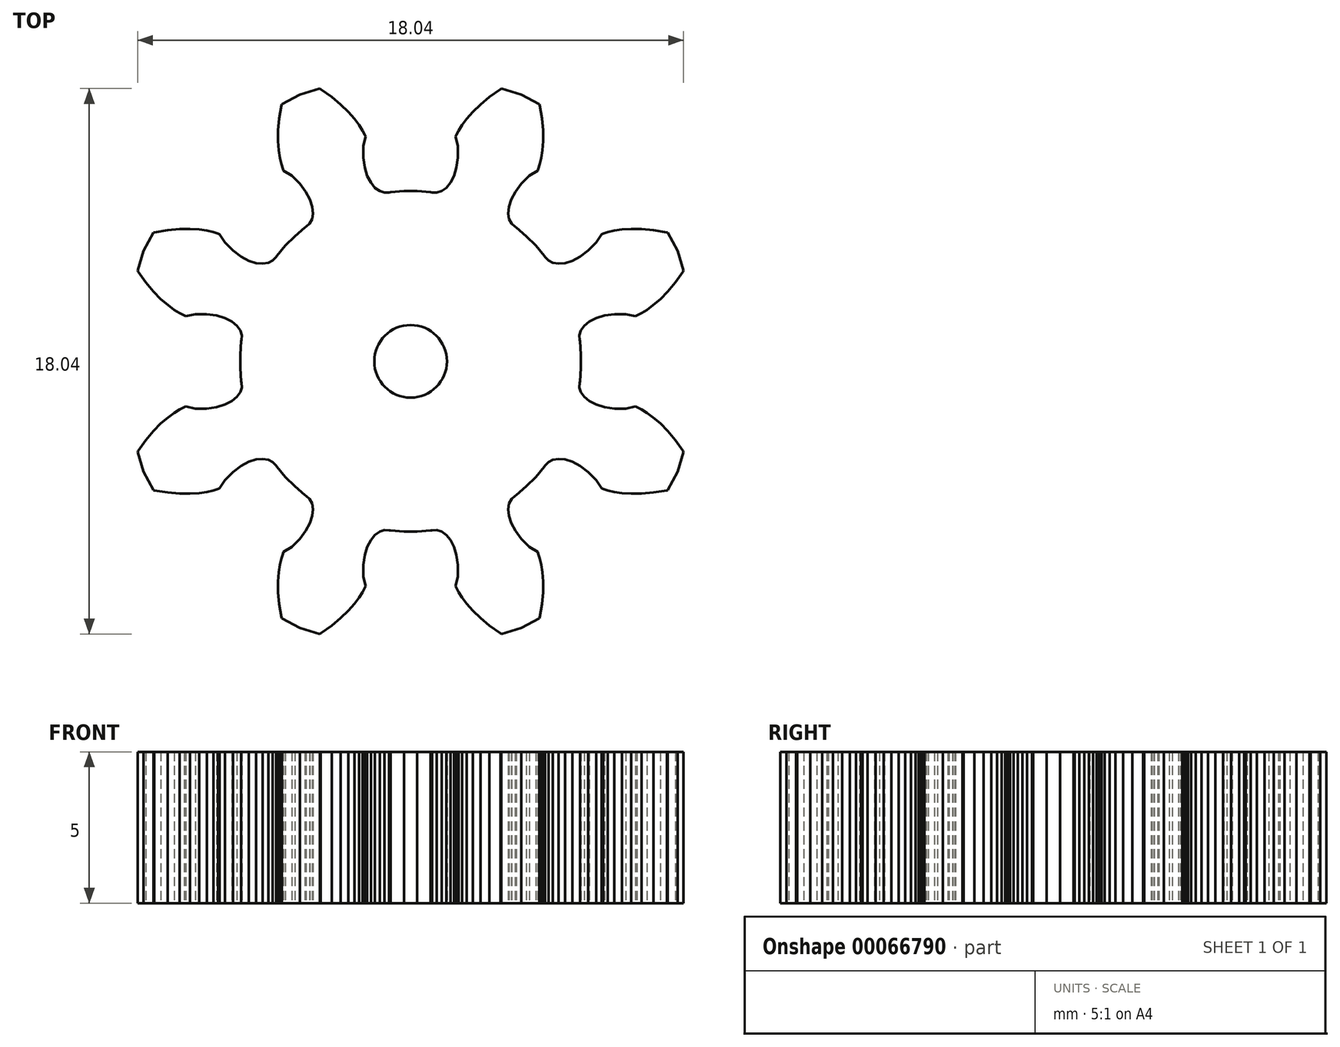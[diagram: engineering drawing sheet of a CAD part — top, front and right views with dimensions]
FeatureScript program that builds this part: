
annotation { "Feature Type Name" : "Feature", "Feature Type Description" : "" }
export const myFeature = defineFeature(function(context is Context, id is Id, definition is map)
    precondition{}
    {
        {
            var Q0;
            Q0=qCreatedBy(makeId("Top.planeOp"),FACE);
            var sketch = newSketch(context, id + "F0", { "sketchPlane" : qUnion([Q0])});
            skCircle(sketch, "E0", {"center": v(0, 0) * mm, "radius": 1.2 * mm});
            skLineSegment(sketch, "E1", {"start": v(-8.5, 4.26) * mm, "end": v(-8.82, 3.65) * mm});
            skLineSegment(sketch, "E2", {"start": v(-8.82, 3.65) * mm, "end": v(-9.02, 3) * mm});
            skLineSegment(sketch, "E3", {"start": v(-9.02, 3) * mm, "end": v(-9, 2.97) * mm});
            skLineSegment(sketch, "E4", {"start": v(-9, 2.97) * mm, "end": v(-8.75, 2.6) * mm});
            skLineSegment(sketch, "E5", {"start": v(-8.75, 2.6) * mm, "end": v(-8.5, 2.3) * mm});
            skLineSegment(sketch, "E6", {"start": v(-8.5, 2.3) * mm, "end": v(-8.25, 2.06) * mm});
            skLineSegment(sketch, "E7", {"start": v(-8.25, 2.06) * mm, "end": v(-8.02, 1.86) * mm});
            skLineSegment(sketch, "E8", {"start": v(-8.02, 1.86) * mm, "end": v(-7.81, 1.7) * mm});
            skLineSegment(sketch, "E9", {"start": v(-7.81, 1.7) * mm, "end": v(-7.63, 1.59) * mm});
            skLineSegment(sketch, "E10", {"start": v(-7.63, 1.59) * mm, "end": v(-7.48, 1.51) * mm});
            skLineSegment(sketch, "E11", {"start": v(-7.48, 1.51) * mm, "end": v(-7.43, 1.5) * mm});
            skLineSegment(sketch, "E12", {"start": v(-7.43, 1.5) * mm, "end": v(-7.11, 1.56) * mm});
            skLineSegment(sketch, "E13", {"start": v(-7.11, 1.56) * mm, "end": v(-6.74, 1.56) * mm});
            skLineSegment(sketch, "E14", {"start": v(-6.74, 1.56) * mm, "end": v(-6.41, 1.52) * mm});
            skLineSegment(sketch, "E15", {"start": v(-6.41, 1.52) * mm, "end": v(-6.13, 1.43) * mm});
            skLineSegment(sketch, "E16", {"start": v(-6.13, 1.43) * mm, "end": v(-5.9, 1.31) * mm});
            skLineSegment(sketch, "E17", {"start": v(-5.9, 1.31) * mm, "end": v(-5.74, 1.18) * mm});
            skLineSegment(sketch, "E18", {"start": v(-5.74, 1.18) * mm, "end": v(-5.63, 1.02) * mm});
            skLineSegment(sketch, "E19", {"start": v(-5.63, 1.02) * mm, "end": v(-5.58, 0.86) * mm});
            skLineSegment(sketch, "E20", {"start": v(-5.58, 0.86) * mm, "end": v(-5.59, 0.7) * mm});
            skLineSegment(sketch, "E21", {"start": v(-5.59, 0.7) * mm, "end": v(-5.6, 0.66) * mm});
            skLineSegment(sketch, "E22", {"start": v(-5.6, 0.66) * mm, "end": v(-5.63, 0.22) * mm});
            skLineSegment(sketch, "E23", {"start": v(-5.63, 0.22) * mm, "end": v(-5.63, -0.22) * mm});
            skLineSegment(sketch, "E24", {"start": v(-5.63, -0.22) * mm, "end": v(-5.6, -0.66) * mm});
            skLineSegment(sketch, "E25", {"start": v(-5.6, -0.66) * mm, "end": v(-5.59, -0.7) * mm});
            skLineSegment(sketch, "E26", {"start": v(-5.59, -0.7) * mm, "end": v(-5.58, -0.86) * mm});
            skLineSegment(sketch, "E27", {"start": v(-5.58, -0.86) * mm, "end": v(-5.63, -1.02) * mm});
            skLineSegment(sketch, "E28", {"start": v(-5.63, -1.02) * mm, "end": v(-5.74, -1.18) * mm});
            skLineSegment(sketch, "E29", {"start": v(-5.74, -1.18) * mm, "end": v(-5.9, -1.31) * mm});
            skLineSegment(sketch, "E30", {"start": v(-5.9, -1.31) * mm, "end": v(-6.13, -1.43) * mm});
            skLineSegment(sketch, "E31", {"start": v(-6.13, -1.43) * mm, "end": v(-6.41, -1.52) * mm});
            skLineSegment(sketch, "E32", {"start": v(-6.41, -1.52) * mm, "end": v(-6.74, -1.56) * mm});
            skLineSegment(sketch, "E33", {"start": v(-6.74, -1.56) * mm, "end": v(-7.11, -1.56) * mm});
            skLineSegment(sketch, "E34", {"start": v(-7.11, -1.56) * mm, "end": v(-7.43, -1.5) * mm});
            skLineSegment(sketch, "E35", {"start": v(-7.43, -1.5) * mm, "end": v(-7.48, -1.51) * mm});
            skLineSegment(sketch, "E36", {"start": v(-7.48, -1.51) * mm, "end": v(-7.63, -1.59) * mm});
            skLineSegment(sketch, "E37", {"start": v(-7.63, -1.59) * mm, "end": v(-7.81, -1.7) * mm});
            skLineSegment(sketch, "E38", {"start": v(-7.81, -1.7) * mm, "end": v(-8.02, -1.86) * mm});
            skLineSegment(sketch, "E39", {"start": v(-8.02, -1.86) * mm, "end": v(-8.25, -2.06) * mm});
            skLineSegment(sketch, "E40", {"start": v(-8.25, -2.06) * mm, "end": v(-8.5, -2.3) * mm});
            skLineSegment(sketch, "E41", {"start": v(-8.5, -2.3) * mm, "end": v(-8.75, -2.6) * mm});
            skLineSegment(sketch, "E42", {"start": v(-8.75, -2.6) * mm, "end": v(-9, -2.97) * mm});
            skLineSegment(sketch, "E43", {"start": v(-9, -2.97) * mm, "end": v(-9.02, -3) * mm});
            skLineSegment(sketch, "E44", {"start": v(-9.02, -3) * mm, "end": v(-8.82, -3.65) * mm});
            skLineSegment(sketch, "E45", {"start": v(-8.82, -3.65) * mm, "end": v(-8.5, -4.26) * mm});
            skLineSegment(sketch, "E46", {"start": v(-8.5, -4.26) * mm, "end": v(-8.46, -4.27) * mm});
            skLineSegment(sketch, "E47", {"start": v(-8.46, -4.27) * mm, "end": v(-8.03, -4.34) * mm});
            skLineSegment(sketch, "E48", {"start": v(-8.03, -4.34) * mm, "end": v(-7.64, -4.38) * mm});
            skLineSegment(sketch, "E49", {"start": v(-7.64, -4.38) * mm, "end": v(-7.29, -4.38) * mm});
            skLineSegment(sketch, "E50", {"start": v(-7.29, -4.38) * mm, "end": v(-6.98, -4.36) * mm});
            skLineSegment(sketch, "E51", {"start": v(-6.98, -4.36) * mm, "end": v(-6.73, -4.32) * mm});
            skLineSegment(sketch, "E52", {"start": v(-6.73, -4.32) * mm, "end": v(-6.52, -4.27) * mm});
            skLineSegment(sketch, "E53", {"start": v(-6.52, -4.27) * mm, "end": v(-6.36, -4.22) * mm});
            skLineSegment(sketch, "E54", {"start": v(-6.36, -4.22) * mm, "end": v(-6.3, -4.2) * mm});
            skLineSegment(sketch, "E55", {"start": v(-6.3, -4.2) * mm, "end": v(-6.14, -3.93) * mm});
            skLineSegment(sketch, "E56", {"start": v(-6.14, -3.93) * mm, "end": v(-5.87, -3.66) * mm});
            skLineSegment(sketch, "E57", {"start": v(-5.87, -3.66) * mm, "end": v(-5.6, -3.46) * mm});
            skLineSegment(sketch, "E58", {"start": v(-5.6, -3.46) * mm, "end": v(-5.35, -3.33) * mm});
            skLineSegment(sketch, "E59", {"start": v(-5.35, -3.33) * mm, "end": v(-5.1, -3.25) * mm});
            skLineSegment(sketch, "E60", {"start": v(-5.1, -3.25) * mm, "end": v(-4.89, -3.23) * mm});
            skLineSegment(sketch, "E61", {"start": v(-4.89, -3.23) * mm, "end": v(-4.7, -3.26) * mm});
            skLineSegment(sketch, "E62", {"start": v(-4.7, -3.26) * mm, "end": v(-4.56, -3.33) * mm});
            skLineSegment(sketch, "E63", {"start": v(-4.56, -3.33) * mm, "end": v(-4.45, -3.45) * mm});
            skLineSegment(sketch, "E64", {"start": v(-4.45, -3.45) * mm, "end": v(-4.42, -3.49) * mm});
            skLineSegment(sketch, "E65", {"start": v(-4.42, -3.49) * mm, "end": v(-4.14, -3.82) * mm});
            skLineSegment(sketch, "E66", {"start": v(-4.14, -3.82) * mm, "end": v(-3.82, -4.14) * mm});
            skLineSegment(sketch, "E67", {"start": v(-3.82, -4.14) * mm, "end": v(-3.49, -4.42) * mm});
            skLineSegment(sketch, "E68", {"start": v(-3.49, -4.42) * mm, "end": v(-3.45, -4.45) * mm});
            skLineSegment(sketch, "E69", {"start": v(-3.45, -4.45) * mm, "end": v(-3.33, -4.56) * mm});
            skLineSegment(sketch, "E70", {"start": v(-3.33, -4.56) * mm, "end": v(-3.26, -4.7) * mm});
            skLineSegment(sketch, "E71", {"start": v(-3.26, -4.7) * mm, "end": v(-3.23, -4.89) * mm});
            skLineSegment(sketch, "E72", {"start": v(-3.23, -4.89) * mm, "end": v(-3.25, -5.1) * mm});
            skLineSegment(sketch, "E73", {"start": v(-3.25, -5.1) * mm, "end": v(-3.33, -5.35) * mm});
            skLineSegment(sketch, "E74", {"start": v(-3.33, -5.35) * mm, "end": v(-3.46, -5.6) * mm});
            skLineSegment(sketch, "E75", {"start": v(-3.46, -5.6) * mm, "end": v(-3.66, -5.87) * mm});
            skLineSegment(sketch, "E76", {"start": v(-3.66, -5.87) * mm, "end": v(-3.93, -6.14) * mm});
            skLineSegment(sketch, "E77", {"start": v(-3.93, -6.14) * mm, "end": v(-4.2, -6.3) * mm});
            skLineSegment(sketch, "E78", {"start": v(-4.2, -6.3) * mm, "end": v(-4.22, -6.36) * mm});
            skLineSegment(sketch, "E79", {"start": v(-4.22, -6.36) * mm, "end": v(-4.27, -6.52) * mm});
            skLineSegment(sketch, "E80", {"start": v(-4.27, -6.52) * mm, "end": v(-4.32, -6.73) * mm});
            skLineSegment(sketch, "E81", {"start": v(-4.32, -6.73) * mm, "end": v(-4.36, -6.98) * mm});
            skLineSegment(sketch, "E82", {"start": v(-4.36, -6.98) * mm, "end": v(-4.38, -7.29) * mm});
            skLineSegment(sketch, "E83", {"start": v(-4.38, -7.29) * mm, "end": v(-4.38, -7.64) * mm});
            skLineSegment(sketch, "E84", {"start": v(-4.38, -7.64) * mm, "end": v(-4.34, -8.03) * mm});
            skLineSegment(sketch, "E85", {"start": v(-4.34, -8.03) * mm, "end": v(-4.27, -8.46) * mm});
            skLineSegment(sketch, "E86", {"start": v(-4.27, -8.46) * mm, "end": v(-4.26, -8.5) * mm});
            skLineSegment(sketch, "E87", {"start": v(-4.26, -8.5) * mm, "end": v(-3.65, -8.82) * mm});
            skLineSegment(sketch, "E88", {"start": v(-3.65, -8.82) * mm, "end": v(-3, -9.02) * mm});
            skLineSegment(sketch, "E89", {"start": v(-3, -9.02) * mm, "end": v(-2.97, -9) * mm});
            skLineSegment(sketch, "E90", {"start": v(-2.97, -9) * mm, "end": v(-2.6, -8.75) * mm});
            skLineSegment(sketch, "E91", {"start": v(-2.6, -8.75) * mm, "end": v(-2.3, -8.5) * mm});
            skLineSegment(sketch, "E92", {"start": v(-2.3, -8.5) * mm, "end": v(-2.06, -8.25) * mm});
            skLineSegment(sketch, "E93", {"start": v(-2.06, -8.25) * mm, "end": v(-1.86, -8.02) * mm});
            skLineSegment(sketch, "E94", {"start": v(-1.86, -8.02) * mm, "end": v(-1.7, -7.81) * mm});
            skLineSegment(sketch, "E95", {"start": v(-1.7, -7.81) * mm, "end": v(-1.59, -7.63) * mm});
            skLineSegment(sketch, "E96", {"start": v(-1.59, -7.63) * mm, "end": v(-1.51, -7.48) * mm});
            skLineSegment(sketch, "E97", {"start": v(-1.51, -7.48) * mm, "end": v(-1.5, -7.43) * mm});
            skLineSegment(sketch, "E98", {"start": v(-1.5, -7.43) * mm, "end": v(-1.56, -7.11) * mm});
            skLineSegment(sketch, "E99", {"start": v(-1.56, -7.11) * mm, "end": v(-1.56, -6.74) * mm});
            skLineSegment(sketch, "E100", {"start": v(-1.56, -6.74) * mm, "end": v(-1.52, -6.41) * mm});
            skLineSegment(sketch, "E101", {"start": v(-1.52, -6.41) * mm, "end": v(-1.43, -6.13) * mm});
            skLineSegment(sketch, "E102", {"start": v(-1.43, -6.13) * mm, "end": v(-1.31, -5.9) * mm});
            skLineSegment(sketch, "E103", {"start": v(-1.31, -5.9) * mm, "end": v(-1.18, -5.74) * mm});
            skLineSegment(sketch, "E104", {"start": v(-1.18, -5.74) * mm, "end": v(-1.02, -5.63) * mm});
            skLineSegment(sketch, "E105", {"start": v(-1.02, -5.63) * mm, "end": v(-0.86, -5.58) * mm});
            skLineSegment(sketch, "E106", {"start": v(-0.86, -5.58) * mm, "end": v(-0.7, -5.59) * mm});
            skLineSegment(sketch, "E107", {"start": v(-0.7, -5.59) * mm, "end": v(-0.66, -5.6) * mm});
            skLineSegment(sketch, "E108", {"start": v(-0.66, -5.6) * mm, "end": v(-0.22, -5.63) * mm});
            skLineSegment(sketch, "E109", {"start": v(-0.22, -5.63) * mm, "end": v(0.22, -5.63) * mm});
            skLineSegment(sketch, "E110", {"start": v(0.22, -5.63) * mm, "end": v(0.66, -5.6) * mm});
            skLineSegment(sketch, "E111", {"start": v(0.66, -5.6) * mm, "end": v(0.7, -5.59) * mm});
            skLineSegment(sketch, "E112", {"start": v(0.7, -5.59) * mm, "end": v(0.86, -5.58) * mm});
            skLineSegment(sketch, "E113", {"start": v(0.86, -5.58) * mm, "end": v(1.02, -5.63) * mm});
            skLineSegment(sketch, "E114", {"start": v(1.02, -5.63) * mm, "end": v(1.18, -5.74) * mm});
            skLineSegment(sketch, "E115", {"start": v(1.18, -5.74) * mm, "end": v(1.31, -5.9) * mm});
            skLineSegment(sketch, "E116", {"start": v(1.31, -5.9) * mm, "end": v(1.43, -6.13) * mm});
            skLineSegment(sketch, "E117", {"start": v(1.43, -6.13) * mm, "end": v(1.52, -6.41) * mm});
            skLineSegment(sketch, "E118", {"start": v(1.52, -6.41) * mm, "end": v(1.56, -6.74) * mm});
            skLineSegment(sketch, "E119", {"start": v(1.56, -6.74) * mm, "end": v(1.56, -7.11) * mm});
            skLineSegment(sketch, "E120", {"start": v(1.56, -7.11) * mm, "end": v(1.5, -7.43) * mm});
            skLineSegment(sketch, "E121", {"start": v(1.5, -7.43) * mm, "end": v(1.51, -7.48) * mm});
            skLineSegment(sketch, "E122", {"start": v(1.51, -7.48) * mm, "end": v(1.59, -7.63) * mm});
            skLineSegment(sketch, "E123", {"start": v(1.59, -7.63) * mm, "end": v(1.7, -7.81) * mm});
            skLineSegment(sketch, "E124", {"start": v(1.7, -7.81) * mm, "end": v(1.86, -8.02) * mm});
            skLineSegment(sketch, "E125", {"start": v(1.86, -8.02) * mm, "end": v(2.06, -8.25) * mm});
            skLineSegment(sketch, "E126", {"start": v(2.06, -8.25) * mm, "end": v(2.3, -8.5) * mm});
            skLineSegment(sketch, "E127", {"start": v(2.3, -8.5) * mm, "end": v(2.6, -8.75) * mm});
            skLineSegment(sketch, "E128", {"start": v(2.6, -8.75) * mm, "end": v(2.97, -9) * mm});
            skLineSegment(sketch, "E129", {"start": v(2.97, -9) * mm, "end": v(3, -9.02) * mm});
            skLineSegment(sketch, "E130", {"start": v(3, -9.02) * mm, "end": v(3.65, -8.82) * mm});
            skLineSegment(sketch, "E131", {"start": v(3.65, -8.82) * mm, "end": v(4.26, -8.5) * mm});
            skLineSegment(sketch, "E132", {"start": v(4.26, -8.5) * mm, "end": v(4.27, -8.46) * mm});
            skLineSegment(sketch, "E133", {"start": v(4.27, -8.46) * mm, "end": v(4.34, -8.03) * mm});
            skLineSegment(sketch, "E134", {"start": v(4.34, -8.03) * mm, "end": v(4.38, -7.64) * mm});
            skLineSegment(sketch, "E135", {"start": v(4.38, -7.64) * mm, "end": v(4.38, -7.29) * mm});
            skLineSegment(sketch, "E136", {"start": v(4.38, -7.29) * mm, "end": v(4.36, -6.98) * mm});
            skLineSegment(sketch, "E137", {"start": v(4.36, -6.98) * mm, "end": v(4.32, -6.73) * mm});
            skLineSegment(sketch, "E138", {"start": v(4.32, -6.73) * mm, "end": v(4.27, -6.52) * mm});
            skLineSegment(sketch, "E139", {"start": v(4.27, -6.52) * mm, "end": v(4.22, -6.36) * mm});
            skLineSegment(sketch, "E140", {"start": v(4.22, -6.36) * mm, "end": v(4.2, -6.3) * mm});
            skLineSegment(sketch, "E141", {"start": v(4.2, -6.3) * mm, "end": v(3.93, -6.14) * mm});
            skLineSegment(sketch, "E142", {"start": v(3.93, -6.14) * mm, "end": v(3.66, -5.87) * mm});
            skLineSegment(sketch, "E143", {"start": v(3.66, -5.87) * mm, "end": v(3.46, -5.6) * mm});
            skLineSegment(sketch, "E144", {"start": v(3.46, -5.6) * mm, "end": v(3.33, -5.35) * mm});
            skLineSegment(sketch, "E145", {"start": v(3.33, -5.35) * mm, "end": v(3.25, -5.1) * mm});
            skLineSegment(sketch, "E146", {"start": v(3.25, -5.1) * mm, "end": v(3.23, -4.89) * mm});
            skLineSegment(sketch, "E147", {"start": v(3.23, -4.89) * mm, "end": v(3.26, -4.7) * mm});
            skLineSegment(sketch, "E148", {"start": v(3.26, -4.7) * mm, "end": v(3.33, -4.56) * mm});
            skLineSegment(sketch, "E149", {"start": v(3.33, -4.56) * mm, "end": v(3.45, -4.45) * mm});
            skLineSegment(sketch, "E150", {"start": v(3.45, -4.45) * mm, "end": v(3.49, -4.42) * mm});
            skLineSegment(sketch, "E151", {"start": v(3.49, -4.42) * mm, "end": v(3.82, -4.14) * mm});
            skLineSegment(sketch, "E152", {"start": v(3.82, -4.14) * mm, "end": v(4.14, -3.82) * mm});
            skLineSegment(sketch, "E153", {"start": v(4.14, -3.82) * mm, "end": v(4.42, -3.49) * mm});
            skLineSegment(sketch, "E154", {"start": v(4.42, -3.49) * mm, "end": v(4.45, -3.45) * mm});
            skLineSegment(sketch, "E155", {"start": v(4.45, -3.45) * mm, "end": v(4.56, -3.33) * mm});
            skLineSegment(sketch, "E156", {"start": v(4.56, -3.33) * mm, "end": v(4.7, -3.26) * mm});
            skLineSegment(sketch, "E157", {"start": v(4.7, -3.26) * mm, "end": v(4.89, -3.23) * mm});
            skLineSegment(sketch, "E158", {"start": v(4.89, -3.23) * mm, "end": v(5.1, -3.25) * mm});
            skLineSegment(sketch, "E159", {"start": v(5.1, -3.25) * mm, "end": v(5.35, -3.33) * mm});
            skLineSegment(sketch, "E160", {"start": v(5.35, -3.33) * mm, "end": v(5.6, -3.46) * mm});
            skLineSegment(sketch, "E161", {"start": v(5.6, -3.46) * mm, "end": v(5.87, -3.66) * mm});
            skLineSegment(sketch, "E162", {"start": v(5.87, -3.66) * mm, "end": v(6.14, -3.93) * mm});
            skLineSegment(sketch, "E163", {"start": v(6.14, -3.93) * mm, "end": v(6.3, -4.2) * mm});
            skLineSegment(sketch, "E164", {"start": v(6.3, -4.2) * mm, "end": v(6.36, -4.22) * mm});
            skLineSegment(sketch, "E165", {"start": v(6.36, -4.22) * mm, "end": v(6.52, -4.27) * mm});
            skLineSegment(sketch, "E166", {"start": v(6.52, -4.27) * mm, "end": v(6.73, -4.32) * mm});
            skLineSegment(sketch, "E167", {"start": v(6.73, -4.32) * mm, "end": v(6.98, -4.36) * mm});
            skLineSegment(sketch, "E168", {"start": v(6.98, -4.36) * mm, "end": v(7.29, -4.38) * mm});
            skLineSegment(sketch, "E169", {"start": v(7.29, -4.38) * mm, "end": v(7.64, -4.38) * mm});
            skLineSegment(sketch, "E170", {"start": v(7.64, -4.38) * mm, "end": v(8.03, -4.34) * mm});
            skLineSegment(sketch, "E171", {"start": v(8.03, -4.34) * mm, "end": v(8.46, -4.27) * mm});
            skLineSegment(sketch, "E172", {"start": v(8.46, -4.27) * mm, "end": v(8.5, -4.26) * mm});
            skLineSegment(sketch, "E173", {"start": v(8.5, -4.26) * mm, "end": v(8.82, -3.65) * mm});
            skLineSegment(sketch, "E174", {"start": v(8.82, -3.65) * mm, "end": v(9.02, -3) * mm});
            skLineSegment(sketch, "E175", {"start": v(9.02, -3) * mm, "end": v(9, -2.97) * mm});
            skLineSegment(sketch, "E176", {"start": v(9, -2.97) * mm, "end": v(8.75, -2.6) * mm});
            skLineSegment(sketch, "E177", {"start": v(8.75, -2.6) * mm, "end": v(8.5, -2.3) * mm});
            skLineSegment(sketch, "E178", {"start": v(8.5, -2.3) * mm, "end": v(8.25, -2.06) * mm});
            skLineSegment(sketch, "E179", {"start": v(8.25, -2.06) * mm, "end": v(8.02, -1.86) * mm});
            skLineSegment(sketch, "E180", {"start": v(8.02, -1.86) * mm, "end": v(7.81, -1.7) * mm});
            skLineSegment(sketch, "E181", {"start": v(7.81, -1.7) * mm, "end": v(7.63, -1.59) * mm});
            skLineSegment(sketch, "E182", {"start": v(7.63, -1.59) * mm, "end": v(7.48, -1.51) * mm});
            skLineSegment(sketch, "E183", {"start": v(7.48, -1.51) * mm, "end": v(7.43, -1.5) * mm});
            skLineSegment(sketch, "E184", {"start": v(7.43, -1.5) * mm, "end": v(7.11, -1.56) * mm});
            skLineSegment(sketch, "E185", {"start": v(7.11, -1.56) * mm, "end": v(6.74, -1.56) * mm});
            skLineSegment(sketch, "E186", {"start": v(6.74, -1.56) * mm, "end": v(6.41, -1.52) * mm});
            skLineSegment(sketch, "E187", {"start": v(6.41, -1.52) * mm, "end": v(6.13, -1.43) * mm});
            skLineSegment(sketch, "E188", {"start": v(6.13, -1.43) * mm, "end": v(5.9, -1.31) * mm});
            skLineSegment(sketch, "E189", {"start": v(5.9, -1.31) * mm, "end": v(5.74, -1.18) * mm});
            skLineSegment(sketch, "E190", {"start": v(5.74, -1.18) * mm, "end": v(5.63, -1.02) * mm});
            skLineSegment(sketch, "E191", {"start": v(5.63, -1.02) * mm, "end": v(5.58, -0.86) * mm});
            skLineSegment(sketch, "E192", {"start": v(5.58, -0.86) * mm, "end": v(5.59, -0.7) * mm});
            skLineSegment(sketch, "E193", {"start": v(5.59, -0.7) * mm, "end": v(5.6, -0.66) * mm});
            skLineSegment(sketch, "E194", {"start": v(5.6, -0.66) * mm, "end": v(5.63, -0.22) * mm});
            skLineSegment(sketch, "E195", {"start": v(5.63, -0.22) * mm, "end": v(5.63, 0.22) * mm});
            skLineSegment(sketch, "E196", {"start": v(5.63, 0.22) * mm, "end": v(5.6, 0.66) * mm});
            skLineSegment(sketch, "E197", {"start": v(5.6, 0.66) * mm, "end": v(5.59, 0.7) * mm});
            skLineSegment(sketch, "E198", {"start": v(5.59, 0.7) * mm, "end": v(5.58, 0.86) * mm});
            skLineSegment(sketch, "E199", {"start": v(5.58, 0.86) * mm, "end": v(5.63, 1.02) * mm});
            skLineSegment(sketch, "E200", {"start": v(5.63, 1.02) * mm, "end": v(5.74, 1.18) * mm});
            skLineSegment(sketch, "E201", {"start": v(5.74, 1.18) * mm, "end": v(5.9, 1.31) * mm});
            skLineSegment(sketch, "E202", {"start": v(5.9, 1.31) * mm, "end": v(6.13, 1.43) * mm});
            skLineSegment(sketch, "E203", {"start": v(6.13, 1.43) * mm, "end": v(6.41, 1.52) * mm});
            skLineSegment(sketch, "E204", {"start": v(6.41, 1.52) * mm, "end": v(6.74, 1.56) * mm});
            skLineSegment(sketch, "E205", {"start": v(6.74, 1.56) * mm, "end": v(7.11, 1.56) * mm});
            skLineSegment(sketch, "E206", {"start": v(7.11, 1.56) * mm, "end": v(7.43, 1.5) * mm});
            skLineSegment(sketch, "E207", {"start": v(7.43, 1.5) * mm, "end": v(7.48, 1.51) * mm});
            skLineSegment(sketch, "E208", {"start": v(7.48, 1.51) * mm, "end": v(7.63, 1.59) * mm});
            skLineSegment(sketch, "E209", {"start": v(7.63, 1.59) * mm, "end": v(7.81, 1.7) * mm});
            skLineSegment(sketch, "E210", {"start": v(7.81, 1.7) * mm, "end": v(8.02, 1.86) * mm});
            skLineSegment(sketch, "E211", {"start": v(8.02, 1.86) * mm, "end": v(8.25, 2.06) * mm});
            skLineSegment(sketch, "E212", {"start": v(8.25, 2.06) * mm, "end": v(8.5, 2.3) * mm});
            skLineSegment(sketch, "E213", {"start": v(8.5, 2.3) * mm, "end": v(8.75, 2.6) * mm});
            skLineSegment(sketch, "E214", {"start": v(8.75, 2.6) * mm, "end": v(9, 2.97) * mm});
            skLineSegment(sketch, "E215", {"start": v(9, 2.97) * mm, "end": v(9.02, 3) * mm});
            skLineSegment(sketch, "E216", {"start": v(9.02, 3) * mm, "end": v(8.82, 3.65) * mm});
            skLineSegment(sketch, "E217", {"start": v(8.82, 3.65) * mm, "end": v(8.5, 4.26) * mm});
            skLineSegment(sketch, "E218", {"start": v(8.5, 4.26) * mm, "end": v(8.46, 4.27) * mm});
            skLineSegment(sketch, "E219", {"start": v(8.46, 4.27) * mm, "end": v(8.03, 4.34) * mm});
            skLineSegment(sketch, "E220", {"start": v(8.03, 4.34) * mm, "end": v(7.64, 4.38) * mm});
            skLineSegment(sketch, "E221", {"start": v(7.64, 4.38) * mm, "end": v(7.29, 4.38) * mm});
            skLineSegment(sketch, "E222", {"start": v(7.29, 4.38) * mm, "end": v(6.98, 4.36) * mm});
            skLineSegment(sketch, "E223", {"start": v(6.98, 4.36) * mm, "end": v(6.73, 4.32) * mm});
            skLineSegment(sketch, "E224", {"start": v(6.73, 4.32) * mm, "end": v(6.52, 4.27) * mm});
            skLineSegment(sketch, "E225", {"start": v(6.52, 4.27) * mm, "end": v(6.36, 4.22) * mm});
            skLineSegment(sketch, "E226", {"start": v(6.36, 4.22) * mm, "end": v(6.3, 4.2) * mm});
            skLineSegment(sketch, "E227", {"start": v(6.3, 4.2) * mm, "end": v(6.14, 3.93) * mm});
            skLineSegment(sketch, "E228", {"start": v(6.14, 3.93) * mm, "end": v(5.87, 3.66) * mm});
            skLineSegment(sketch, "E229", {"start": v(5.87, 3.66) * mm, "end": v(5.6, 3.46) * mm});
            skLineSegment(sketch, "E230", {"start": v(5.6, 3.46) * mm, "end": v(5.35, 3.33) * mm});
            skLineSegment(sketch, "E231", {"start": v(5.35, 3.33) * mm, "end": v(5.1, 3.25) * mm});
            skLineSegment(sketch, "E232", {"start": v(5.1, 3.25) * mm, "end": v(4.89, 3.23) * mm});
            skLineSegment(sketch, "E233", {"start": v(4.89, 3.23) * mm, "end": v(4.7, 3.26) * mm});
            skLineSegment(sketch, "E234", {"start": v(4.7, 3.26) * mm, "end": v(4.56, 3.33) * mm});
            skLineSegment(sketch, "E235", {"start": v(4.56, 3.33) * mm, "end": v(4.45, 3.45) * mm});
            skLineSegment(sketch, "E236", {"start": v(4.45, 3.45) * mm, "end": v(4.42, 3.49) * mm});
            skLineSegment(sketch, "E237", {"start": v(4.42, 3.49) * mm, "end": v(4.14, 3.82) * mm});
            skLineSegment(sketch, "E238", {"start": v(4.14, 3.82) * mm, "end": v(3.82, 4.14) * mm});
            skLineSegment(sketch, "E239", {"start": v(3.82, 4.14) * mm, "end": v(3.49, 4.42) * mm});
            skLineSegment(sketch, "E240", {"start": v(3.49, 4.42) * mm, "end": v(3.45, 4.45) * mm});
            skLineSegment(sketch, "E241", {"start": v(3.45, 4.45) * mm, "end": v(3.33, 4.56) * mm});
            skLineSegment(sketch, "E242", {"start": v(3.33, 4.56) * mm, "end": v(3.26, 4.7) * mm});
            skLineSegment(sketch, "E243", {"start": v(3.26, 4.7) * mm, "end": v(3.23, 4.89) * mm});
            skLineSegment(sketch, "E244", {"start": v(3.23, 4.89) * mm, "end": v(3.25, 5.1) * mm});
            skLineSegment(sketch, "E245", {"start": v(3.25, 5.1) * mm, "end": v(3.33, 5.35) * mm});
            skLineSegment(sketch, "E246", {"start": v(3.33, 5.35) * mm, "end": v(3.46, 5.6) * mm});
            skLineSegment(sketch, "E247", {"start": v(3.46, 5.6) * mm, "end": v(3.66, 5.87) * mm});
            skLineSegment(sketch, "E248", {"start": v(3.66, 5.87) * mm, "end": v(3.93, 6.14) * mm});
            skLineSegment(sketch, "E249", {"start": v(3.93, 6.14) * mm, "end": v(4.2, 6.3) * mm});
            skLineSegment(sketch, "E250", {"start": v(4.2, 6.3) * mm, "end": v(4.22, 6.36) * mm});
            skLineSegment(sketch, "E251", {"start": v(4.22, 6.36) * mm, "end": v(4.27, 6.52) * mm});
            skLineSegment(sketch, "E252", {"start": v(4.27, 6.52) * mm, "end": v(4.32, 6.73) * mm});
            skLineSegment(sketch, "E253", {"start": v(4.32, 6.73) * mm, "end": v(4.36, 6.98) * mm});
            skLineSegment(sketch, "E254", {"start": v(4.36, 6.98) * mm, "end": v(4.38, 7.29) * mm});
            skLineSegment(sketch, "E255", {"start": v(4.38, 7.29) * mm, "end": v(4.38, 7.64) * mm});
            skLineSegment(sketch, "E256", {"start": v(4.38, 7.64) * mm, "end": v(4.34, 8.03) * mm});
            skLineSegment(sketch, "E257", {"start": v(4.34, 8.03) * mm, "end": v(4.27, 8.46) * mm});
            skLineSegment(sketch, "E258", {"start": v(4.27, 8.46) * mm, "end": v(4.26, 8.5) * mm});
            skLineSegment(sketch, "E259", {"start": v(4.26, 8.5) * mm, "end": v(3.65, 8.82) * mm});
            skLineSegment(sketch, "E260", {"start": v(3.65, 8.82) * mm, "end": v(3, 9.02) * mm});
            skLineSegment(sketch, "E261", {"start": v(3, 9.02) * mm, "end": v(2.97, 9) * mm});
            skLineSegment(sketch, "E262", {"start": v(2.97, 9) * mm, "end": v(2.6, 8.75) * mm});
            skLineSegment(sketch, "E263", {"start": v(2.6, 8.75) * mm, "end": v(2.3, 8.5) * mm});
            skLineSegment(sketch, "E264", {"start": v(2.3, 8.5) * mm, "end": v(2.06, 8.25) * mm});
            skLineSegment(sketch, "E265", {"start": v(2.06, 8.25) * mm, "end": v(1.86, 8.02) * mm});
            skLineSegment(sketch, "E266", {"start": v(1.86, 8.02) * mm, "end": v(1.7, 7.81) * mm});
            skLineSegment(sketch, "E267", {"start": v(1.7, 7.81) * mm, "end": v(1.59, 7.63) * mm});
            skLineSegment(sketch, "E268", {"start": v(1.59, 7.63) * mm, "end": v(1.51, 7.48) * mm});
            skLineSegment(sketch, "E269", {"start": v(1.51, 7.48) * mm, "end": v(1.5, 7.43) * mm});
            skLineSegment(sketch, "E270", {"start": v(1.5, 7.43) * mm, "end": v(1.56, 7.11) * mm});
            skLineSegment(sketch, "E271", {"start": v(1.56, 7.11) * mm, "end": v(1.56, 6.74) * mm});
            skLineSegment(sketch, "E272", {"start": v(1.56, 6.74) * mm, "end": v(1.52, 6.41) * mm});
            skLineSegment(sketch, "E273", {"start": v(1.52, 6.41) * mm, "end": v(1.43, 6.13) * mm});
            skLineSegment(sketch, "E274", {"start": v(1.43, 6.13) * mm, "end": v(1.31, 5.9) * mm});
            skLineSegment(sketch, "E275", {"start": v(1.31, 5.9) * mm, "end": v(1.18, 5.74) * mm});
            skLineSegment(sketch, "E276", {"start": v(1.18, 5.74) * mm, "end": v(1.02, 5.63) * mm});
            skLineSegment(sketch, "E277", {"start": v(1.02, 5.63) * mm, "end": v(0.86, 5.58) * mm});
            skLineSegment(sketch, "E278", {"start": v(0.86, 5.58) * mm, "end": v(0.7, 5.59) * mm});
            skLineSegment(sketch, "E279", {"start": v(0.7, 5.59) * mm, "end": v(0.66, 5.6) * mm});
            skLineSegment(sketch, "E280", {"start": v(0.66, 5.6) * mm, "end": v(0.22, 5.63) * mm});
            skLineSegment(sketch, "E281", {"start": v(0.22, 5.63) * mm, "end": v(-0.22, 5.63) * mm});
            skLineSegment(sketch, "E282", {"start": v(-0.22, 5.63) * mm, "end": v(-0.66, 5.6) * mm});
            skLineSegment(sketch, "E283", {"start": v(-0.66, 5.6) * mm, "end": v(-0.7, 5.59) * mm});
            skLineSegment(sketch, "E284", {"start": v(-0.7, 5.59) * mm, "end": v(-0.86, 5.58) * mm});
            skLineSegment(sketch, "E285", {"start": v(-0.86, 5.58) * mm, "end": v(-1.02, 5.63) * mm});
            skLineSegment(sketch, "E286", {"start": v(-1.02, 5.63) * mm, "end": v(-1.18, 5.74) * mm});
            skLineSegment(sketch, "E287", {"start": v(-1.18, 5.74) * mm, "end": v(-1.31, 5.9) * mm});
            skLineSegment(sketch, "E288", {"start": v(-1.31, 5.9) * mm, "end": v(-1.43, 6.13) * mm});
            skLineSegment(sketch, "E289", {"start": v(-1.43, 6.13) * mm, "end": v(-1.52, 6.41) * mm});
            skLineSegment(sketch, "E290", {"start": v(-1.52, 6.41) * mm, "end": v(-1.56, 6.74) * mm});
            skLineSegment(sketch, "E291", {"start": v(-1.56, 6.74) * mm, "end": v(-1.56, 7.11) * mm});
            skLineSegment(sketch, "E292", {"start": v(-1.56, 7.11) * mm, "end": v(-1.5, 7.43) * mm});
            skLineSegment(sketch, "E293", {"start": v(-1.5, 7.43) * mm, "end": v(-1.51, 7.48) * mm});
            skLineSegment(sketch, "E294", {"start": v(-1.51, 7.48) * mm, "end": v(-1.59, 7.63) * mm});
            skLineSegment(sketch, "E295", {"start": v(-1.59, 7.63) * mm, "end": v(-1.7, 7.81) * mm});
            skLineSegment(sketch, "E296", {"start": v(-1.7, 7.81) * mm, "end": v(-1.86, 8.02) * mm});
            skLineSegment(sketch, "E297", {"start": v(-1.86, 8.02) * mm, "end": v(-2.06, 8.25) * mm});
            skLineSegment(sketch, "E298", {"start": v(-2.06, 8.25) * mm, "end": v(-2.3, 8.5) * mm});
            skLineSegment(sketch, "E299", {"start": v(-2.3, 8.5) * mm, "end": v(-2.6, 8.75) * mm});
            skLineSegment(sketch, "E300", {"start": v(-2.6, 8.75) * mm, "end": v(-2.97, 9) * mm});
            skLineSegment(sketch, "E301", {"start": v(-2.97, 9) * mm, "end": v(-3, 9.02) * mm});
            skLineSegment(sketch, "E302", {"start": v(-3, 9.02) * mm, "end": v(-3.65, 8.82) * mm});
            skLineSegment(sketch, "E303", {"start": v(-3.65, 8.82) * mm, "end": v(-4.26, 8.5) * mm});
            skLineSegment(sketch, "E304", {"start": v(-4.26, 8.5) * mm, "end": v(-4.27, 8.46) * mm});
            skLineSegment(sketch, "E305", {"start": v(-4.27, 8.46) * mm, "end": v(-4.34, 8.03) * mm});
            skLineSegment(sketch, "E306", {"start": v(-4.34, 8.03) * mm, "end": v(-4.38, 7.64) * mm});
            skLineSegment(sketch, "E307", {"start": v(-4.38, 7.64) * mm, "end": v(-4.38, 7.29) * mm});
            skLineSegment(sketch, "E308", {"start": v(-4.38, 7.29) * mm, "end": v(-4.36, 6.98) * mm});
            skLineSegment(sketch, "E309", {"start": v(-4.36, 6.98) * mm, "end": v(-4.32, 6.73) * mm});
            skLineSegment(sketch, "E310", {"start": v(-4.32, 6.73) * mm, "end": v(-4.27, 6.52) * mm});
            skLineSegment(sketch, "E311", {"start": v(-4.27, 6.52) * mm, "end": v(-4.22, 6.36) * mm});
            skLineSegment(sketch, "E312", {"start": v(-4.22, 6.36) * mm, "end": v(-4.2, 6.3) * mm});
            skLineSegment(sketch, "E313", {"start": v(-4.2, 6.3) * mm, "end": v(-3.93, 6.14) * mm});
            skLineSegment(sketch, "E314", {"start": v(-3.93, 6.14) * mm, "end": v(-3.66, 5.87) * mm});
            skLineSegment(sketch, "E315", {"start": v(-3.66, 5.87) * mm, "end": v(-3.46, 5.6) * mm});
            skLineSegment(sketch, "E316", {"start": v(-3.46, 5.6) * mm, "end": v(-3.33, 5.35) * mm});
            skLineSegment(sketch, "E317", {"start": v(-3.33, 5.35) * mm, "end": v(-3.25, 5.1) * mm});
            skLineSegment(sketch, "E318", {"start": v(-3.25, 5.1) * mm, "end": v(-3.23, 4.89) * mm});
            skLineSegment(sketch, "E319", {"start": v(-3.23, 4.89) * mm, "end": v(-3.26, 4.7) * mm});
            skLineSegment(sketch, "E320", {"start": v(-3.26, 4.7) * mm, "end": v(-3.33, 4.56) * mm});
            skLineSegment(sketch, "E321", {"start": v(-3.33, 4.56) * mm, "end": v(-3.45, 4.45) * mm});
            skLineSegment(sketch, "E322", {"start": v(-3.45, 4.45) * mm, "end": v(-3.49, 4.42) * mm});
            skLineSegment(sketch, "E323", {"start": v(-3.49, 4.42) * mm, "end": v(-3.82, 4.14) * mm});
            skLineSegment(sketch, "E324", {"start": v(-3.82, 4.14) * mm, "end": v(-4.14, 3.82) * mm});
            skLineSegment(sketch, "E325", {"start": v(-4.14, 3.82) * mm, "end": v(-4.42, 3.49) * mm});
            skLineSegment(sketch, "E326", {"start": v(-4.42, 3.49) * mm, "end": v(-4.45, 3.45) * mm});
            skLineSegment(sketch, "E327", {"start": v(-4.45, 3.45) * mm, "end": v(-4.56, 3.33) * mm});
            skLineSegment(sketch, "E328", {"start": v(-4.56, 3.33) * mm, "end": v(-4.7, 3.26) * mm});
            skLineSegment(sketch, "E329", {"start": v(-4.7, 3.26) * mm, "end": v(-4.89, 3.23) * mm});
            skLineSegment(sketch, "E330", {"start": v(-4.89, 3.23) * mm, "end": v(-5.1, 3.25) * mm});
            skLineSegment(sketch, "E331", {"start": v(-5.1, 3.25) * mm, "end": v(-5.35, 3.33) * mm});
            skLineSegment(sketch, "E332", {"start": v(-5.35, 3.33) * mm, "end": v(-5.6, 3.46) * mm});
            skLineSegment(sketch, "E333", {"start": v(-5.6, 3.46) * mm, "end": v(-5.87, 3.66) * mm});
            skLineSegment(sketch, "E334", {"start": v(-5.87, 3.66) * mm, "end": v(-6.14, 3.93) * mm});
            skLineSegment(sketch, "E335", {"start": v(-6.14, 3.93) * mm, "end": v(-6.3, 4.2) * mm});
            skLineSegment(sketch, "E336", {"start": v(-6.3, 4.2) * mm, "end": v(-6.36, 4.22) * mm});
            skLineSegment(sketch, "E337", {"start": v(-6.36, 4.22) * mm, "end": v(-6.52, 4.27) * mm});
            skLineSegment(sketch, "E338", {"start": v(-6.52, 4.27) * mm, "end": v(-6.73, 4.32) * mm});
            skLineSegment(sketch, "E339", {"start": v(-6.73, 4.32) * mm, "end": v(-6.98, 4.36) * mm});
            skLineSegment(sketch, "E340", {"start": v(-6.98, 4.36) * mm, "end": v(-7.29, 4.38) * mm});
            skLineSegment(sketch, "E341", {"start": v(-7.29, 4.38) * mm, "end": v(-7.64, 4.38) * mm});
            skLineSegment(sketch, "E342", {"start": v(-7.64, 4.38) * mm, "end": v(-8.03, 4.34) * mm});
            skLineSegment(sketch, "E343", {"start": v(-8.03, 4.34) * mm, "end": v(-8.46, 4.27) * mm});
            skLineSegment(sketch, "E344", {"start": v(-8.46, 4.27) * mm, "end": v(-8.5, 4.26) * mm});
            skSolve(sketch);
        }
        {
            var Q0;
            Q0=makeQuery(id+"F0.imprint","IMPRINT",FACE,{"disambiguationData":[TD([[makeQuery(id+"F0.imprint","IMPRINT",EDGE,{"derivedFrom":sQuery(id+"F0.wireOp",EDGE,"E0")}),-1.0]])]});
            extrude(context, id + "F1", {"entities" : qUnion([Q0]), "depth" : 5 * mm});
        }
    });
